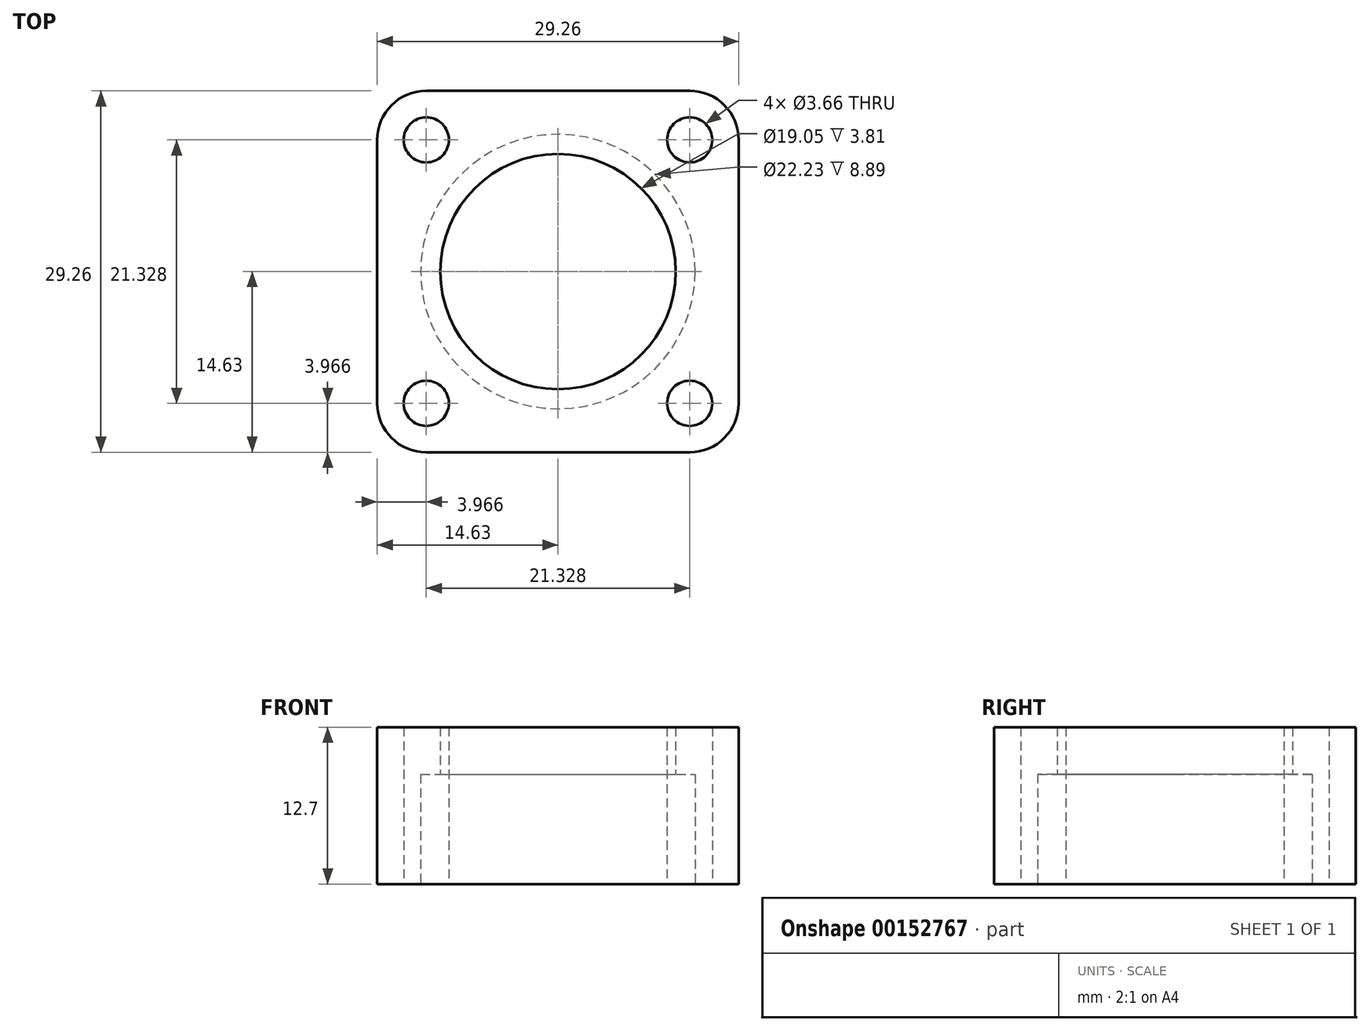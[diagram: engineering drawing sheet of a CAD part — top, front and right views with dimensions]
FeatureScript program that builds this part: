
annotation { "Feature Type Name" : "Feature", "Feature Type Description" : "" }
export const myFeature = defineFeature(function(context is Context, id is Id, definition is map)
    precondition{}
    {
        {
            var Q0;
            Q0=qCreatedBy(makeId("Top.planeOp"),FACE);
            var sketch = newSketch(context, id + "F0", { "sketchPlane" : qUnion([Q0])});
            skCircle(sketch, "E0", {"center": v(0, 0) * mm, "radius": 11.11 * mm, "construction": true});
            skLineSegment(sketch, "E1", {"start": v(0, 0) * mm, "end": v(0, -14.63) * mm, "construction": true});
            skLineSegment(sketch, "E2.bottom", {"start": v(14.63, -14.63) * mm, "end": v(-14.63, -14.63) * mm});
            skLineSegment(sketch, "E2.top", {"start": v(14.63, 14.63) * mm, "end": v(-14.63, 14.63) * mm});
            skLineSegment(sketch, "E2.left", {"start": v(14.63, -14.63) * mm, "end": v(14.63, 14.63) * mm});
            skLineSegment(sketch, "E2.right", {"start": v(-14.63, -14.63) * mm, "end": v(-14.63, 14.63) * mm});
            skLineSegment(sketch, "E3.bottom", {"start": v(-10.66, 10.66) * mm, "end": v(10.66, 10.66) * mm, "construction": true});
            skLineSegment(sketch, "E3.top", {"start": v(-10.66, -10.66) * mm, "end": v(10.66, -10.66) * mm, "construction": true});
            skLineSegment(sketch, "E3.left", {"start": v(-10.66, 10.66) * mm, "end": v(-10.66, -10.66) * mm, "construction": true});
            skLineSegment(sketch, "E3.right", {"start": v(10.66, 10.66) * mm, "end": v(10.66, -10.66) * mm, "construction": true});
            skCircle(sketch, "E4", {"center": v(-10.66, 10.66) * mm, "radius": 3.97 * mm, "construction": true});
            skLineSegment(sketch, "E5", {"start": v(0, 0) * mm, "end": v(0, 14.63) * mm, "construction": true});
            skCircle(sketch, "E6", {"center": v(-10.66, 10.66) * mm, "radius": 1.83 * mm});
            skCircle(sketch, "E7", {"center": v(10.66, 10.66) * mm, "radius": 1.83 * mm});
            skCircle(sketch, "E8", {"center": v(10.66, -10.66) * mm, "radius": 1.83 * mm});
            skCircle(sketch, "E9", {"center": v(-10.66, -10.66) * mm, "radius": 1.83 * mm});
            skCircle(sketch, "E10", {"center": v(0, 0) * mm, "radius": 9.53 * mm});
            skSolve(sketch);
        }
        {
            var Q0;
            Q0=qSketchRegion(id+"F0",true);
            extrude(context, id + "F1", {"entities" : qUnion([Q0]), "depth" : 12.7 * mm});
        }
        {
            var Q0;
            Q0=makeQuery(id+"F1.opExtrude","SWEPT_EDGE",EDGE,{"disambiguationData":[OSD([sQuery(id+"F0.wireOp",EDGE,"E2.top"),sQuery(id+"F0.wireOp",EDGE,"E2.right")])]});
            var Q1;
            Q1=makeQuery(id+"F1.opExtrude","SWEPT_EDGE",EDGE,{"disambiguationData":[OSD([sQuery(id+"F0.wireOp",EDGE,"E2.bottom"),sQuery(id+"F0.wireOp",EDGE,"E2.right")])]});
            var Q2;
            Q2=makeQuery(id+"F1.opExtrude","SWEPT_EDGE",EDGE,{"disambiguationData":[OSD([sQuery(id+"F0.wireOp",EDGE,"E2.bottom"),sQuery(id+"F0.wireOp",EDGE,"E2.left")])]});
            var Q3;
            Q3=makeQuery(id+"F1.opExtrude","SWEPT_EDGE",EDGE,{"disambiguationData":[OSD([sQuery(id+"F0.wireOp",EDGE,"E2.top"),sQuery(id+"F0.wireOp",EDGE,"E2.left")])]});
            fillet(context, id + "F2", {"entities" : qUnion([Q0, Q1, Q2, Q3]), "radius" : 3.97 * mm, "tangentPropagation" : true, "allowEdgeOverflow" : false});
        }
        {
            var Q0;
            Q0=makeQuery(id+"F1.opExtrude","CAP_FACE",FACE,{"disambiguationData":[OSD([sQuery(id+"F0.wireOp",EDGE,"E2.bottom"),sQuery(id+"F0.wireOp",EDGE,"E2.top"),sQuery(id+"F0.wireOp",EDGE,"E2.left"),sQuery(id+"F0.wireOp",EDGE,"E2.right"),sQuery(id+"F0.wireOp",EDGE,"E6"),sQuery(id+"F0.wireOp",EDGE,"E7"),sQuery(id+"F0.wireOp",EDGE,"E8"),sQuery(id+"F0.wireOp",EDGE,"E9"),sQuery(id+"F0.wireOp",EDGE,"E10")])],"isStart":true});
            var sketch = newSketch(context, id + "F3", { "sketchPlane" : qUnion([Q0])});
            skCircle(sketch, "E11", {"center": v(0, 0) * mm, "radius": 11.11 * mm});
            skSolve(sketch);
        }
        {
            var Q0;
            Q0=qSketchRegion(id+"F3",true);
            extrude(context, id + "F4", {"entities" : qUnion([Q0]), "operationType" : NewBodyOperationType.REMOVE, "oppositeDirection" : true, "depth" : 8.9 * mm});
        }
    });
